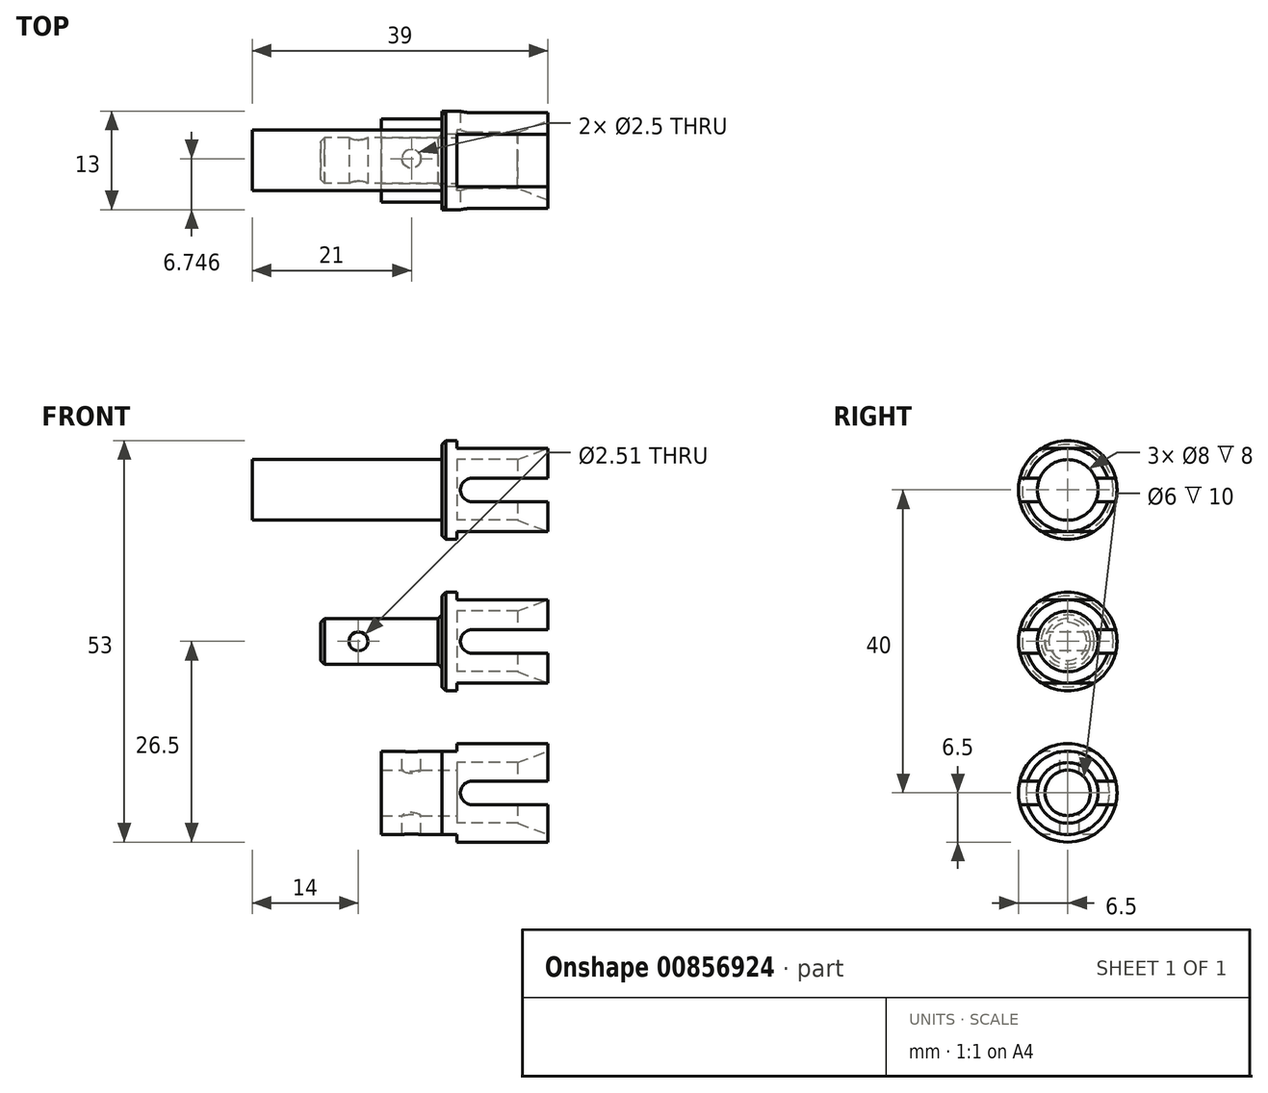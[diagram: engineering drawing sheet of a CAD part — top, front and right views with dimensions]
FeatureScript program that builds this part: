
annotation { "Feature Type Name" : "Feature", "Feature Type Description" : "" }
export const myFeature = defineFeature(function(context is Context, id is Id, definition is map)
    precondition{}
    {
        {
            var Q0;
            Q0=qCreatedBy(makeId("Front.planeOp"),FACE);
            var sketch = newSketch(context, id + "F0", { "sketchPlane" : qUnion([Q0])});
            skLineSegment(sketch, "E0", {"start": v(0, 0) * mm, "end": v(0, 5.7) * mm, "construction": true});
            skLineSegment(sketch, "E1", {"start": v(0, 0) * mm, "end": v(14.57, 0) * mm, "construction": true});
            skLineSegment(sketch, "E2", {"start": v(11, 4) * mm, "end": v(11, 6.5) * mm});
            skLineSegment(sketch, "E3", {"start": v(11, 6.5) * mm, "end": v(-3, 6.5) * mm});
            skLineSegment(sketch, "E4", {"start": v(-3, 6.5) * mm, "end": v(-3, 3) * mm});
            skLineSegment(sketch, "E5", {"start": v(-3, 3) * mm, "end": v(-19, 3) * mm});
            skLineSegment(sketch, "E6", {"start": v(-19, 3) * mm, "end": v(-19, 0) * mm});
            skLineSegment(sketch, "E7", {"start": v(-19, 0) * mm, "end": v(-1, 0) * mm});
            skLineSegment(sketch, "E8", {"start": v(-1, 0) * mm, "end": v(-1, 4) * mm});
            skLineSegment(sketch, "E9", {"start": v(-1, 4) * mm, "end": v(11, 4) * mm});
            skSolve(sketch);
        }
        {
            var Q0;
            Q0=makeQuery(id+"F0.imprint","IMPRINT",FACE,{"disambiguationData":[TD([[makeQuery(id+"F0.imprint","IMPRINT",EDGE,{"derivedFrom":sQuery(id+"F0.wireOp",EDGE,"E2")}),1.0]])]});
            var Q1;
            Q1=sQuery(id+"F0.wireOp",EDGE,"E1");
            revolve(context, id + "F1", {"surfaceOperationType" : NewSurfaceOperationType.NEW, "entities" : qUnion([Q0]), "axis" : qUnion([Q1]), "revolveType" : RevolveType.FULL});
        }
        {
            var Q0;
            Q0=qCreatedBy(makeId("Front.planeOp"),FACE);
            var sketch = newSketch(context, id + "F2", { "sketchPlane" : qUnion([Q0])});
            skLineSegment(sketch, "E10", {"start": v(1, 0) * mm, "end": v(11, 0) * mm, "construction": true});
            skArc(sketch, "E11.0.startCap", {"start": v(1, -1.55) * mm, "mid": v(-0.55, 0) * mm, "end": v(1, 1.55) * mm});
            skArc(sketch, "E11.0.endCap", {"start": v(11, 1.55) * mm, "mid": v(12.55, 0) * mm, "end": v(11, -1.55) * mm});
            skLineSegment(sketch, "E11.0.left", {"start": v(1, 1.55) * mm, "end": v(11, 1.55) * mm});
            skLineSegment(sketch, "E11.0.right", {"start": v(1, -1.55) * mm, "end": v(11, -1.55) * mm});
            skCircle(sketch, "E12", {"center": v(-14, 0) * mm, "radius": 1.25 * mm});
            skSolve(sketch);
        }
        {
            var Q0;
            Q0=makeQuery(id+"F1.opRevolve","SWEPT_EDGE",EDGE,{"disambiguationData":[OSD([sQuery(id+"F0.wireOp",EDGE,"E2"),sQuery(id+"F0.wireOp",EDGE,"E9")])]});
            chamfer(context, id + "F3", {"entities" : qUnion([Q0]), "chamferType" : ChamferType.TWO_OFFSETS, "width1" : 1.5 * mm, "oppositeDirection" : false, "width2" : 4 * mm, "tangentPropagation" : true});
        }
        {
            var Q0;
            Q0 = qSketchRegion(id + "F2", true);
            extrude(context, id + "F4", {"entities" : qUnion([Q0]), "operationType" : NewBodyOperationType.REMOVE, "oppositeDirection" : true, "depth" : 25 * mm, "offsetDistance" : 25 * mm, "symmetric" : true});
        }
        {
            var Q0;
            Q0=qCreatedBy(makeId("Front.planeOp"),FACE);
            var sketch = newSketch(context, id + "F5", { "sketchPlane" : qUnion([Q0])});
            skLineSegment(sketch, "E13", {"start": v(-3, 6.5) * mm, "end": v(11, 6.5) * mm, "construction": true});
            skLineSegment(sketch, "E14", {"start": v(11, -6.5) * mm, "end": v(-3, -6.5) * mm, "construction": true});
            skLineSegment(sketch, "E15.bottom", {"start": v(11, -6.5) * mm, "end": v(-1, -6.5) * mm});
            skLineSegment(sketch, "E15.top", {"start": v(11, -5.5) * mm, "end": v(-1, -5.5) * mm});
            skLineSegment(sketch, "E15.left", {"start": v(11, -6.5) * mm, "end": v(11, -5.5) * mm});
            skLineSegment(sketch, "E15.right", {"start": v(-1, -6.5) * mm, "end": v(-1, -5.5) * mm});
            skLineSegment(sketch, "E16.bottom", {"start": v(11, 6.5) * mm, "end": v(-1, 6.5) * mm});
            skLineSegment(sketch, "E16.top", {"start": v(11, 5.5) * mm, "end": v(-1, 5.5) * mm});
            skLineSegment(sketch, "E16.left", {"start": v(11, 6.5) * mm, "end": v(11, 5.5) * mm});
            skLineSegment(sketch, "E16.right", {"start": v(-1, 6.5) * mm, "end": v(-1, 5.5) * mm});
            skLineSegment(sketch, "E17", {"start": v(0, 0) * mm, "end": v(13.93, 0) * mm, "construction": true});
            skSolve(sketch);
        }
        {
            var Q0;
            Q0=makeQuery(id+"F1.opRevolve","SWEPT_BODY",BODY,{"disambiguationData":[OSD([sQuery(id+"F0.wireOp",EDGE,"E2"),sQuery(id+"F0.wireOp",EDGE,"E3"),sQuery(id+"F0.wireOp",EDGE,"E4"),sQuery(id+"F0.wireOp",EDGE,"E5"),sQuery(id+"F0.wireOp",EDGE,"E6"),sQuery(id+"F0.wireOp",EDGE,"E7"),sQuery(id+"F0.wireOp",EDGE,"E8"),sQuery(id+"F0.wireOp",EDGE,"E9")])]});
            transform(context, id + "F6", {"entities" : qUnion([Q0]), "transformType" : TransformType.TRANSLATION_3D, "dx" : 0 * mm, "dy" : 0 * mm, "dz" : -20 * mm, "makeCopy" : true});
        }
        {
            var Q0;
            Q0 = qSketchRegion(id + "F5", true);
            extrude(context, id + "F7", {"entities" : qUnion([Q0]), "operationType" : NewBodyOperationType.REMOVE, "oppositeDirection" : true, "depth" : 25 * mm, "offsetDistance" : 25 * mm, "symmetric" : true});
        }
        {
            var Q0;
            Q0=makeQuery(id+"F1.opRevolve","SWEPT_EDGE",EDGE,{"disambiguationData":[OSD([sQuery(id+"F0.wireOp",EDGE,"E5"),sQuery(id+"F0.wireOp",EDGE,"E6")])]});
            var Q1;
            Q1=makeQuery(id+"F1.opRevolve","SWEPT_EDGE",EDGE,{"disambiguationData":[OSD([sQuery(id+"F0.wireOp",EDGE,"E3"),sQuery(id+"F0.wireOp",EDGE,"E4")])]});
            chamfer(context, id + "F8", {"entities" : qUnion([Q0, Q1]), "width" : 0.5 * mm, "tangentPropagation" : true});
        }
        {
            var Q0;
            Q0=makeQuery(id+"F1.opRevolve","SWEPT_EDGE",EDGE,{"disambiguationData":[OSD([sQuery(id+"F0.wireOp",EDGE,"E4"),sQuery(id+"F0.wireOp",EDGE,"E5")])]});
            chamfer(context, id + "F9", {"entities" : qUnion([Q0]), "width" : 0.5 * mm, "tangentPropagation" : true});
        }
        {
            var Q0;
            Q0=makeQuery(id+"F6.opPattern","COPY",FACE,{"derivedFrom":makeQuery(id+"F1.opRevolve","SWEPT_FACE",FACE,{"disambiguationData":[OSD([sQuery(id+"F0.wireOp",EDGE,"E6")])]}),"instanceName":"1"});
            var Q1;
            Q1=makeQuery(id+"F6.opPattern","COPY",FACE,{"derivedFrom":makeQuery(id+"F1.opRevolve","SWEPT_FACE",FACE,{"disambiguationData":[OSD([sQuery(id+"F0.wireOp",EDGE,"E4")])]}),"instanceName":"1"});
            extrude(context, id + "F10", {"entities" : qUnion([Q0]), "operationType" : NewBodyOperationType.REMOVE, "endBound" : BoundingType.UP_TO_SURFACE, "oppositeDirection" : true, "depth" : 25 * mm, "endBoundEntityFace" : qUnion([Q1]), "offsetDistance" : 25 * mm});
        }
        {
            var Q0;
            {var subQ0=sQuery(id+"F0.wireOp",EDGE,"E4");Q0=makeQuery(id+"F10.boolean.opBoolean","MERGE",FACE,{"derivedFrom":[makeQuery(id+"F6.opPattern","COPY",FACE,{"derivedFrom":makeQuery(id+"F1.opRevolve","SWEPT_FACE",FACE,{"disambiguationData":[OSD([subQ0])]}),"instanceName":"1"}),makeQuery(id+"F10.opExtrude","CAP_FACE",FACE,{"disambiguationData":[OSD([subQ0])],"isStart":false})]});}
            extrude(context, id + "F11", {"entities" : qUnion([Q0]), "operationType" : NewBodyOperationType.ADD, "depth" : 8 * mm, "offsetDistance" : 25 * mm});
        }
        {
            var Q0;
            Q0=makeQuery(id+"F11.opExtrude","CAP_FACE",FACE,{"disambiguationData":[OSD([sQuery(id+"F0.wireOp",EDGE,"E4")])],"isStart":false});
            var sketch = newSketch(context, id + "F12", { "sketchPlane" : qUnion([Q0])});
            skPoint(sketch, "E18", {"position": v(0, -20) * mm});
            skSolve(sketch);
        }
        {
            var Q0;
            Q0=sQuery(id+"F12.wireOp",VERTEX,"E18");
            var Q1;
            Q1=makeQuery(id+"F6.opPattern","COPY",BODY,{"derivedFrom":makeQuery(id+"F1.opRevolve","SWEPT_BODY",BODY,{"disambiguationData":[OSD([sQuery(id+"F0.wireOp",EDGE,"E2"),sQuery(id+"F0.wireOp",EDGE,"E3"),sQuery(id+"F0.wireOp",EDGE,"E4"),sQuery(id+"F0.wireOp",EDGE,"E5"),sQuery(id+"F0.wireOp",EDGE,"E6"),sQuery(id+"F0.wireOp",EDGE,"E7"),sQuery(id+"F0.wireOp",EDGE,"E8"),sQuery(id+"F0.wireOp",EDGE,"E9")])]}),"instanceName":"1"});
            hole(context, id + "F13", {"style" : HoleStyle.SIMPLE, "endStyle" : HoleEndStyle.THROUGH, "holeDiameter" : 6 * mm, "majorDiameter" : 5 * mm, "isTappedThrough" : true, "tappedDepth" : 12 * mm, "tapClearance" : 3, "locations" : qUnion([Q0]), "scope" : qUnion([Q1])});
        }
        {
            var Q0;
            Q0=makeQuery(id+"F11.opExtrude","CAP_FACE",FACE,{"disambiguationData":[OSD([sQuery(id+"F0.wireOp",EDGE,"E4")])],"isStart":false});
            var sketch = newSketch(context, id + "F14", { "sketchPlane" : qUnion([Q0])});
            skCircle(sketch, "E19", {"center": v(0, -20) * mm, "radius": 5.5 * mm});
            skCircle(sketch, "E20", {"center": v(0, -20) * mm, "radius": 6.5 * mm});
            skSolve(sketch);
        }
        {
            var Q0;
            Q0 = qSketchRegion(id + "F14", true);
            extrude(context, id + "F15", {"entities" : qUnion([Q0]), "operationType" : NewBodyOperationType.REMOVE, "oppositeDirection" : true, "depth" : 8 * mm, "offsetDistance" : 25 * mm});
        }
        {
            var Q0;
            Q0=qCreatedBy(makeId("Top.planeOp"),FACE);
            cPlane(context, id + "F16", {"entities" : qUnion([Q0]), "cplaneType" : CPlaneType.OFFSET, "offset" : 20 * mm, "oppositeDirection" : true, "width" : 150 * mm, "height" : 150 * mm});
        }
        {
            var Q0;
            Q0=qCreatedBy(id+"F16.planeOp",FACE);
            var sketch = newSketch(context, id + "F17", { "sketchPlane" : qUnion([Q0])});
            skCircle(sketch, "E21", {"center": v(-7, 0.25) * mm, "radius": 1.25 * mm});
            skSolve(sketch);
        }
        {
            var Q0;
            Q0=qCreatedBy(makeId("Front.planeOp"),FACE);
            var sketch = newSketch(context, id + "F18", { "sketchPlane" : qUnion([Q0])});
            skLineSegment(sketch, "E22", {"start": v(-11, -14.5) * mm, "end": v(-3, -14.5) * mm, "construction": true});
            skLineSegment(sketch, "E23.0", {"start": v(-3, -26.5) * mm, "end": v(-3, -13.5) * mm, "construction": true});
            skLineSegment(sketch, "E24.bottom", {"start": v(-3, -14.5) * mm, "end": v(-1, -14.5) * mm});
            skLineSegment(sketch, "E24.top", {"start": v(-3, -13.5) * mm, "end": v(-1, -13.5) * mm});
            skLineSegment(sketch, "E24.left", {"start": v(-3, -14.5) * mm, "end": v(-3, -13.5) * mm});
            skLineSegment(sketch, "E24.right", {"start": v(-1, -14.5) * mm, "end": v(-1, -13.5) * mm});
            skLineSegment(sketch, "E25", {"start": v(-3, -25.5) * mm, "end": v(-11, -25.5) * mm, "construction": true});
            skLineSegment(sketch, "E26.bottom", {"start": v(-3, -25.5) * mm, "end": v(-1, -25.5) * mm});
            skLineSegment(sketch, "E26.top", {"start": v(-3, -26.5) * mm, "end": v(-1, -26.5) * mm});
            skLineSegment(sketch, "E26.left", {"start": v(-3, -25.5) * mm, "end": v(-3, -26.5) * mm});
            skLineSegment(sketch, "E26.right", {"start": v(-1, -25.5) * mm, "end": v(-1, -26.5) * mm});
            skSolve(sketch);
        }
        {
            var Q0;
            Q0 = qSketchRegion(id + "F18", true);
            extrude(context, id + "F19", {"entities" : qUnion([Q0]), "operationType" : NewBodyOperationType.REMOVE, "oppositeDirection" : true, "depth" : 25 * mm, "offsetDistance" : 25 * mm, "symmetric" : true});
        }
        {
            var Q0;
            Q0 = qSketchRegion(id + "F17", true);
            extrude(context, id + "F20", {"entities" : qUnion([Q0]), "operationType" : NewBodyOperationType.REMOVE, "oppositeDirection" : true, "depth" : 25 * mm, "offsetDistance" : 25 * mm, "symmetric" : true});
        }
        {
            var Q0;
            Q0=makeQuery(id+"F1.opRevolve","SWEPT_BODY",BODY,{"disambiguationData":[OSD([sQuery(id+"F0.wireOp",EDGE,"E2"),sQuery(id+"F0.wireOp",EDGE,"E3"),sQuery(id+"F0.wireOp",EDGE,"E4"),sQuery(id+"F0.wireOp",EDGE,"E5"),sQuery(id+"F0.wireOp",EDGE,"E6"),sQuery(id+"F0.wireOp",EDGE,"E7"),sQuery(id+"F0.wireOp",EDGE,"E8"),sQuery(id+"F0.wireOp",EDGE,"E9")])]});
            transform(context, id + "F21", {"entities" : qUnion([Q0]), "transformType" : TransformType.TRANSLATION_3D, "dx" : 0 * mm, "dy" : 0 * mm, "dz" : 20 * mm, "makeCopy" : true});
        }
        {
            var Q0;
            Q0=makeQuery(id+"F21.opPattern","COPY",FACE,{"derivedFrom":makeQuery(id+"F1.opRevolve","SWEPT_FACE",FACE,{"disambiguationData":[OSD([sQuery(id+"F0.wireOp",EDGE,"E4")])]}),"instanceName":"1"});
            var sketch = newSketch(context, id + "F22", { "sketchPlane" : qUnion([Q0])});
            skCircle(sketch, "E27", {"center": v(0, 20) * mm, "radius": 4 * mm});
            skSolve(sketch);
        }
        {
            var Q0;
            Q0 = qSketchRegion(id + "F22", true);
            extrude(context, id + "F23", {"entities" : qUnion([Q0]), "operationType" : NewBodyOperationType.ADD, "depth" : 25 * mm, "offsetDistance" : 25 * mm});
        }
    });
